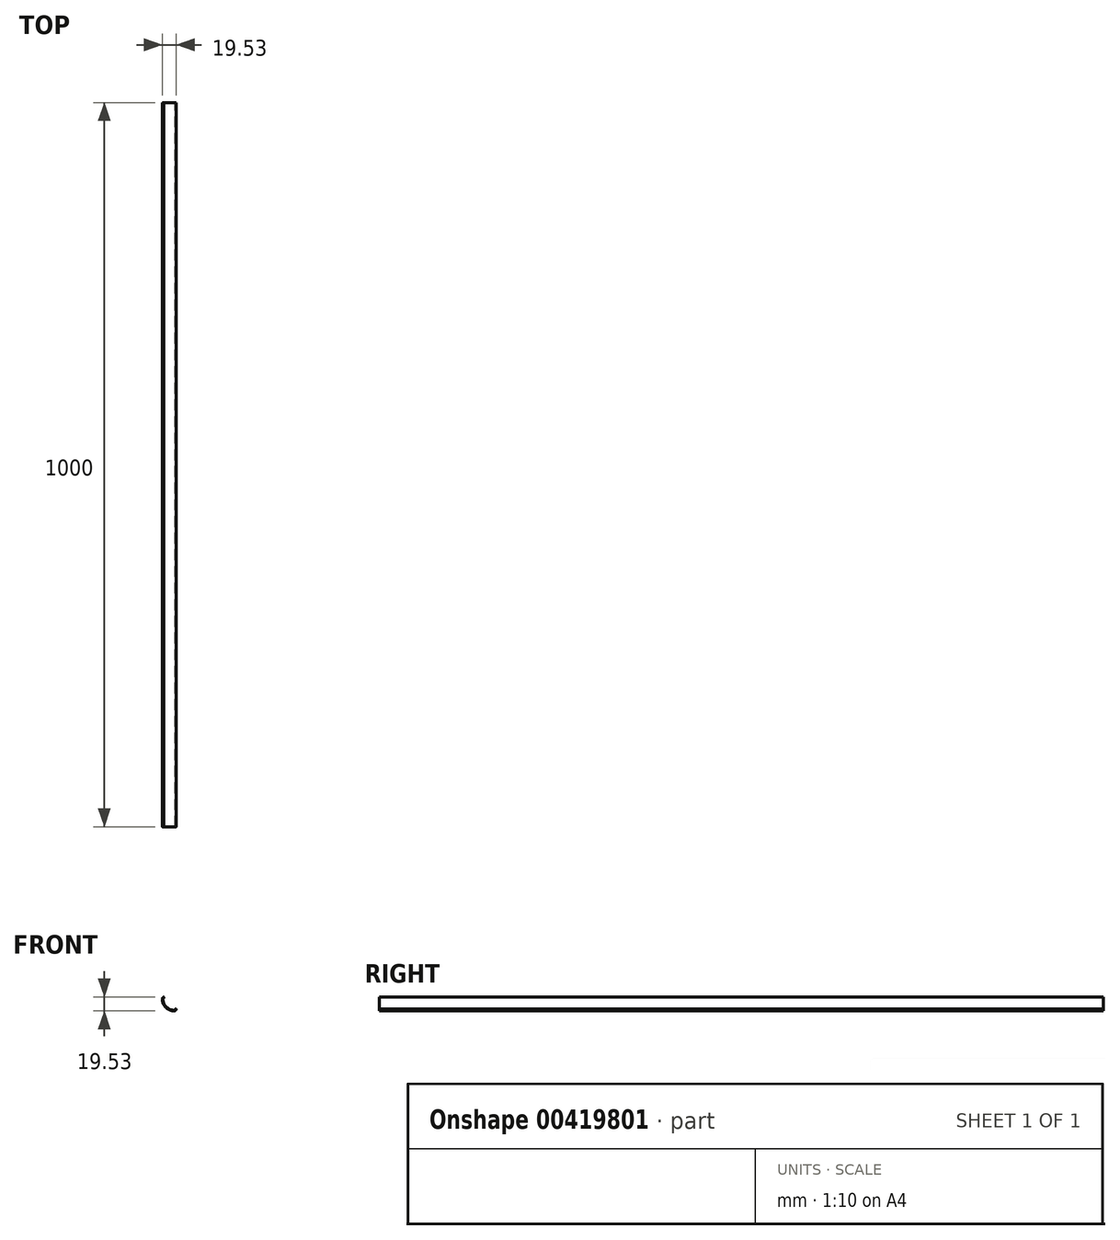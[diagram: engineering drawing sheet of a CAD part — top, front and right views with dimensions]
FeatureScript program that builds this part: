
annotation { "Feature Type Name" : "Feature", "Feature Type Description" : "" }
export const myFeature = defineFeature(function(context is Context, id is Id, definition is map)
    precondition{}
    {
        {
            var Q0;
            Q0=qCreatedBy(makeId("Front.planeOp"),FACE);
            var sketch = newSketch(context, id + "F0", { "sketchPlane" : qUnion([Q0])});
            skArc(sketch, "E0", {"start": v(-7.5, 8.45) * mm, "mid": v(-8, 8.95) * mm, "end": v(-8.5, 8.45) * mm});
            skArc(sketch, "E1", {"start": v(9, -9.05) * mm, "mid": v(9.5, -8.55) * mm, "end": v(9, -8.05) * mm});
            skLineSegment(sketch, "E2", {"start": v(-8.5, 8.45) * mm, "end": v(-8.5, 7.95) * mm});
            skLineSegment(sketch, "E3", {"start": v(-9, 7.45) * mm, "end": v(-9.52, 7.45) * mm});
            skLineSegment(sketch, "E4", {"start": v(9, -9.05) * mm, "end": v(8.5, -9.05) * mm});
            skLineSegment(sketch, "E5", {"start": v(8, -9.55) * mm, "end": v(8, -10.07) * mm});
            skArc(sketch, "E6", {"start": v(-10.02, 6.97) * mm, "mid": v(-5.05, -5.6) * mm, "end": v(7.52, -10.57) * mm});
            skArc(sketch, "E7.0", {"start": v(-9.03, 6) * mm, "mid": v(-4.34, -4.9) * mm, "end": v(6.54, -9.58) * mm});
            skPoint(sketch, "E8.visualSharp", {"position": v(8, -9.05) * mm});
            skArc(sketch, "E8.filletArc", {"start": v(8.5, -9.05) * mm, "mid": v(8.15, -9.2) * mm, "end": v(8, -9.55) * mm});
            skPoint(sketch, "E9.visualSharp", {"position": v(-8.5, 7.45) * mm});
            skArc(sketch, "E9.filletArc", {"start": v(-9, 7.45) * mm, "mid": v(-8.65, 7.6) * mm, "end": v(-8.5, 7.95) * mm});
            skArc(sketch, "E10.0", {"start": v(-8.64, 6.5) * mm, "mid": v(-7.82, 7.02) * mm, "end": v(-7.5, 7.95) * mm});
            skArc(sketch, "E11.0", {"start": v(8.5, -8.05) * mm, "mid": v(7.57, -8.37) * mm, "end": v(7.04, -9.2) * mm});
            skLineSegment(sketch, "E12", {"start": v(7, -9.55) * mm, "end": v(7, -9.58) * mm});
            skLineSegment(sketch, "E13", {"start": v(8.5, -8.05) * mm, "end": v(9, -8.05) * mm});
            skLineSegment(sketch, "E14", {"start": v(-9, 6.45) * mm, "end": v(-9.03, 6.45) * mm});
            skLineSegment(sketch, "E15", {"start": v(-7.5, 7.95) * mm, "end": v(-7.5, 8.45) * mm});
            skPoint(sketch, "E16.visualSharp", {"position": v(-10, 7.45) * mm});
            skArc(sketch, "E16.filletArc", {"start": v(-9.52, 7.45) * mm, "mid": v(-9.87, 7.3) * mm, "end": v(-10.02, 6.97) * mm});
            skPoint(sketch, "E17.visualSharp", {"position": v(8, -10.55) * mm});
            skArc(sketch, "E17.filletArc", {"start": v(7.52, -10.57) * mm, "mid": v(7.86, -10.42) * mm, "end": v(8, -10.07) * mm});
            skArc(sketch, "E18.filletArc", {"start": v(6.54, -9.58) * mm, "mid": v(6.86, -9.47) * mm, "end": v(7.04, -9.2) * mm});
            skArc(sketch, "E19.filletArc", {"start": v(-8.64, 6.5) * mm, "mid": v(-8.92, 6.31) * mm, "end": v(-9.03, 6) * mm});
            skSolve(sketch);
        }
        {
            var Q0;
            Q0=makeQuery(id+"F0.imprint","IMPRINT",FACE,{"disambiguationData":[TD([[makeQuery(id+"F0.imprint","IMPRINT",EDGE,{"derivedFrom":sQuery(id+"F0.wireOp",EDGE,"E0")}),1.0]])]});
            extrude(context, id + "F1", {"entities" : qUnion([Q0]), "depth" : 1000 * mm});
        }
    });
